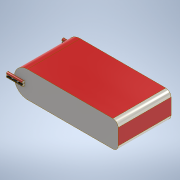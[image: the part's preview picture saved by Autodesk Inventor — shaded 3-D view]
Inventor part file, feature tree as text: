
AUTODESK INVENTOR PART (.ipt)
format: ipt  version: 2022 (Build 260153000, 153)  size: 216,064 bytes
history: native  units: mm
features: extrude x5, sketch x5, fillet x1
ambient origin geometry x8: Origin, YZ Plane, XZ Plane, XY Plane, X Axis, Y Axis, Z Axis, Center Point
bodies: Solid1 (feature_tree)
feature tree (11):
  extrude  "Extrusion1"  TaperAngle=0.0deg  [1 undecoded]
  extrude  "Extrusion2"  TaperAngle=0.0deg  [1 undecoded]
  extrude  "Extrusion3"  Depth=3.0mm
  extrude  "Extrusion4"  Depth=53.0mm
  extrude  "Extrusion5"  Depth=1.5mm TaperAngle=0.0deg
  fillet  "Fillet1"  Radius=0.75mm
  sketch  "Sketch2"  dims[d0=15.0mm d1=0.0mm]
  sketch  "Sketch3"  dims[d2=51.5mm d3=0.0mm]
  sketch  "Sketch4"  dims[d4=30.0mm d5=0.0mm d6=3.0mm]
  sketch  "Sketch5"  dims[d7=6.0mm d8=53.0mm]
  sketch  "Sketch6"  dims[d9=10.5mm d10=1.5mm d11=0.0mm d12=0.75mm d13=0.75mm d14=0.0mm d15=0.0mm d16=4.5mm d17=53.0mm d18=5.25mm d19=0.0mm d20=1.5mm d21=0.0mm d22=1.5mm d23=0.75mm d24=0.75mm d25=1.5mm d26=0.0mm d27=0.0mm d28=3.0mm]
note: 2 required parameter values undecoded (feature->parameter linkage not recoverable at this tier; creation-order binding heuristic only, values carry confidence <= 0.55)
